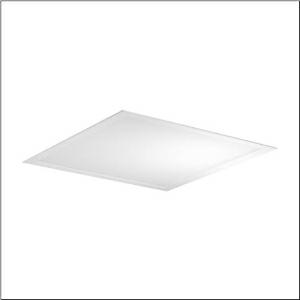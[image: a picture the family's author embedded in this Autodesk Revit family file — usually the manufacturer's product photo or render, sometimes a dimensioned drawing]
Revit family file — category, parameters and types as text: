
# Revit family: apollon_21_square_51mq11w72414
name_source: partatom
category: Lighting Fixtures
units: mm (PartAtom-declared; Revit-internal decimal feet)

## family parameters
Cut with Voids When Loaded = No
Host = Face
Light Source = No
Part Type = Normal
Room Calculation Point = No
Round Connector Dimension = Use Diameter
Shared = No

## types (1)
- Apollon 21 square (1 x LED, 4200 lm, 23.3 W, 4000K)
    Apparent Load = 23 VA
    CIE Flux Codes = 60 87 97 100 100
    Color Rendering = 80
    Color Temperature = 4000K
    Default Elevation = 1800 mm
    Description = Apollon 21 square, office luminaire, primary optical cover: micro prismatic cover, of PMMA, CAT 2 (L<= 3000cd/m²), light emission: direct distribution, primary light characteristic: symmetric, installation type: lay-in mounting, LED, rated luminous flux: 4.200lm, luminous efficacy: 180lm/W, light colour: 840, colour temperature: 4000K, control gear: ON/OFF, with terminal, 3-pole, mains connection: 220..240V, AC/DC, 0/50..60Hz, rated input power: 23.3W, housing, of aluminium, coated, traffic white (RAL 9016), module: M625, length: 620mm, width: 620mm, height: 55mm, recess depth: 180mm, housing upper side, of sheet steel, galvanised, protection rating (complete): IP20, protection rating (lamp compartment, on room side): IP50, insulation class (complete): insulation class II (safety insulation), certification: CE, ENEC, impact resistance: IK03, permissible operating ambient temperature: -20..+45°C, permissible storage temperature: -40..+80°C, standard: EN 60598-2-22, packaging unit: 1 piece
    Height = 0 mm  [stored 0 ft]
    Lamp = 1 x LED
    Lamp Light Flux = 4200 lm
    Lamp Power = 23.3 W
    Lamp count = 1
    Length = 620 mm
    Luminous efficacy = 180 lm/W
    Manufacturer = Siteco
    ModVariant = No
    Model = 51MQ11W72414
    Mounting Place = Ceiling
    Mounting Type = Recessed
    Number of Poles = 1
    OnlyDefault = Yes
    Power Factor = 1
    Product Name = Apollon 21 square
    Product group = office luminaire | ceiling recessed
    ProductGroupID = 401
    Protection Class = Protection class II
    Protection Degree = IP 20
    RLX_Detail_Level = 1
    RLX_Emergency_Light_Flux = 0 lm
    RLX_Emergency_Type = 0
    RLX_Emergency_Type_DB = No
    RlxData = <blob elided: 13013 chars, md5=06f7a087>
    Socket = socket
    Standby Power = 0 W
    System Light Flux = 4200 lm
    System Power = 23 W
    Type Comments = Product without accessories
    Type Image = l_1291054.jpg
    URL = http://relux.com
    VarID = ---
    Voltage = 0 V
    Weight = 0.00 kg
    Width = 620 mm

note: [stored X ft] marks values corroborated as IEEE doubles in the binary element streams (Revit-internal decimal feet)

## geometry (parser evidence)
native form markers: Sweep x10
no freeform markers — native parametric forms only
